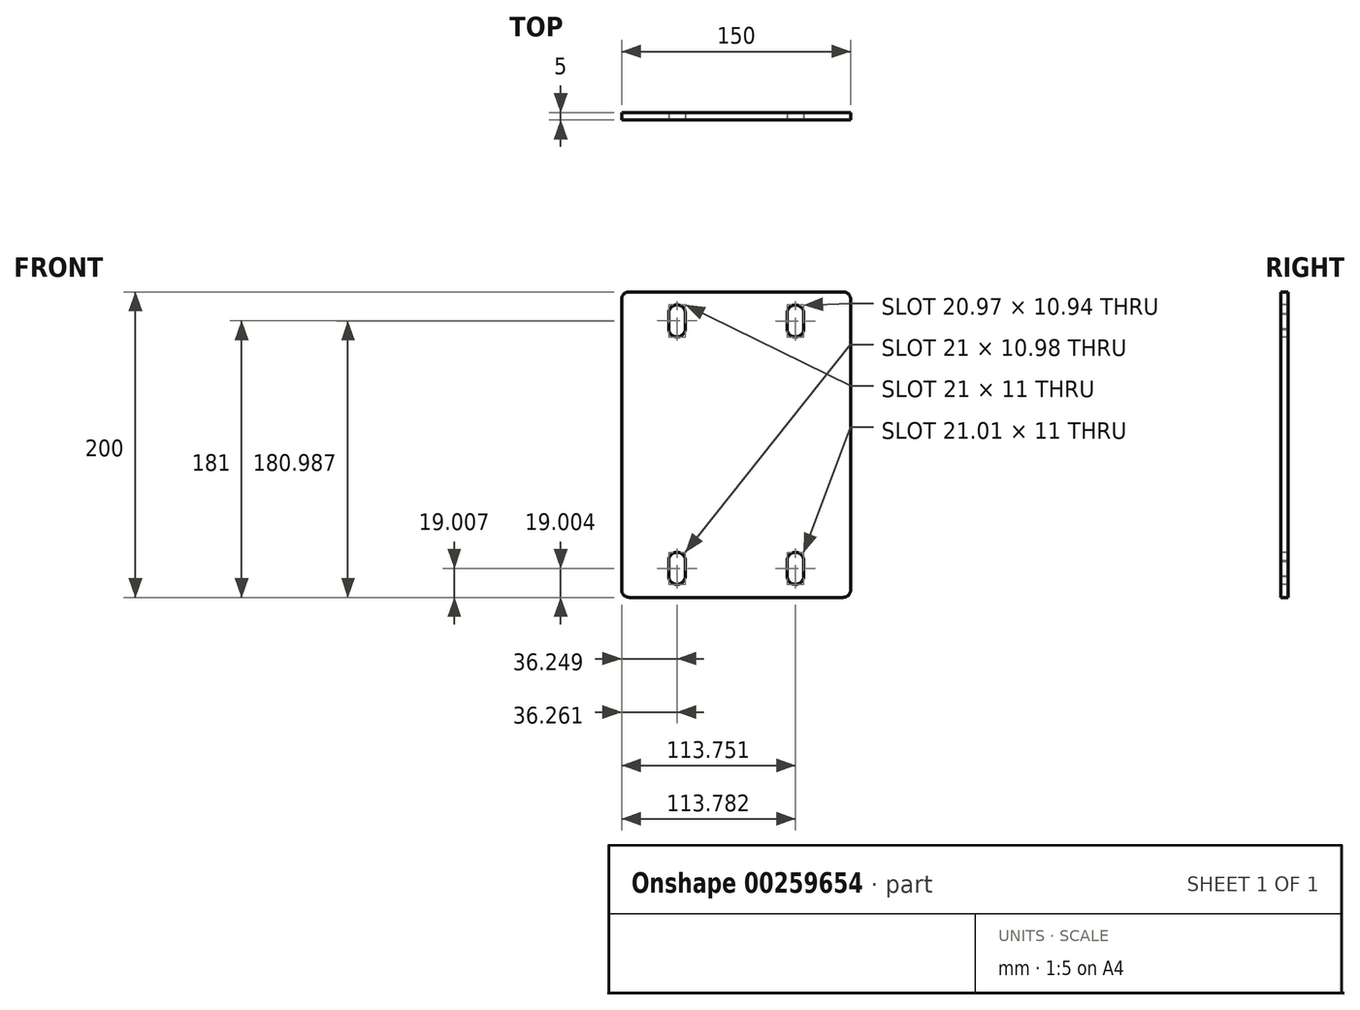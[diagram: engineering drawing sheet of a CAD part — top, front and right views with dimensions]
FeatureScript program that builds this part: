
annotation { "Feature Type Name" : "Feature", "Feature Type Description" : "" }
export const myFeature = defineFeature(function(context is Context, id is Id, definition is map)
    precondition{}
    {
        {
            var Q0;
            Q0=qCreatedBy(makeId("Front.planeOp"),FACE);
            var sketch = newSketch(context, id + "F0", { "sketchPlane" : qUnion([Q0])});
            skLineSegment(sketch, "E0.rect.bottom", {"start": v(-70, 100) * mm, "end": v(70, 100) * mm});
            skLineSegment(sketch, "E0.rect.top", {"start": v(-70, -100) * mm, "end": v(70, -100) * mm});
            skLineSegment(sketch, "E0.rect.left", {"start": v(-75, 95) * mm, "end": v(-75, -95) * mm});
            skLineSegment(sketch, "E0.rect.right", {"start": v(75, 95) * mm, "end": v(75, -95) * mm});
            skPoint(sketch, "E1.visualSharp", {"position": v(-75, 100) * mm});
            skArc(sketch, "E1.filletArc", {"start": v(-70, 100) * mm, "mid": v(-73.54, 98.54) * mm, "end": v(-75, 95) * mm});
            skPoint(sketch, "E2.visualSharp", {"position": v(-75, -100) * mm});
            skArc(sketch, "E2.filletArc", {"start": v(-75, -95) * mm, "mid": v(-73.54, -98.54) * mm, "end": v(-70, -100) * mm});
            skPoint(sketch, "E3.visualSharp", {"position": v(75, -100) * mm});
            skArc(sketch, "E3.filletArc", {"start": v(70, -100) * mm, "mid": v(73.54, -98.54) * mm, "end": v(75, -95) * mm});
            skPoint(sketch, "E4.visualSharp", {"position": v(75, 100) * mm});
            skArc(sketch, "E4.filletArc", {"start": v(75, 95) * mm, "mid": v(73.54, 98.54) * mm, "end": v(70, 100) * mm});
            skSolve(sketch);
        }
        {
            var Q0;
            Q0=qSketchRegion(id+"F0",true);
            extrude(context, id + "F1", {"entities" : qUnion([Q0]), "depth" : 5 * mm});
        }
        {
            var Q0;
            Q0=makeQuery(id+"F1.opExtrude","CAP_FACE",FACE,{"disambiguationData":[OSD([sQuery(id+"F0.wireOp",EDGE,"E0.rect.bottom"),sQuery(id+"F0.wireOp",EDGE,"E0.rect.top"),sQuery(id+"F0.wireOp",EDGE,"E0.rect.left"),sQuery(id+"F0.wireOp",EDGE,"E0.rect.right"),sQuery(id+"F0.wireOp",EDGE,"E1.filletArc"),sQuery(id+"F0.wireOp",EDGE,"E2.filletArc"),sQuery(id+"F0.wireOp",EDGE,"E3.filletArc"),sQuery(id+"F0.wireOp",EDGE,"E4.filletArc")])],"isStart":false});
            var sketch = newSketch(context, id + "F2", { "sketchPlane" : qUnion([Q0])});
            skLineSegment(sketch, "E5.rect.right", {"start": v(38.75, 86) * mm, "end": v(38.76, 85.98) * mm});
            skPoint(sketch, "E5.rect.middle", {"position": v(0, 0) * mm});
            skLineSegment(sketch, "E6", {"start": v(-44.24, 75.72) * mm, "end": v(-44.25, 86) * mm});
            skLineSegment(sketch, "E7", {"start": v(-33.25, 86) * mm, "end": v(-33.25, 76) * mm});
            skArc(sketch, "E8.trimOffspring", {"start": v(-44.24, 76.28) * mm, "mid": v(-38.89, 70.5) * mm, "end": v(-33.25, 76) * mm});
            skArc(sketch, "E9.trimOffspring", {"start": v(-33.25, 86) * mm, "mid": v(-38.75, 91.5) * mm, "end": v(-44.25, 86) * mm});
            skArc(sketch, "E10", {"start": v(33.31, 76.82) * mm, "mid": v(38.33, 70.5) * mm, "end": v(44.25, 75.99) * mm});
            skArc(sketch, "E11", {"start": v(33.25, -85.89) * mm, "mid": v(38.7, -91.5) * mm, "end": v(44.25, -86) * mm});
            skArc(sketch, "E12", {"start": v(-44.23, -85.51) * mm, "mid": v(-39, -91.5) * mm, "end": v(-33.25, -86) * mm});
            skLineSegment(sketch, "E13", {"start": v(-44.23, -76.5) * mm, "end": v(-44.23, -86.49) * mm});
            skLineSegment(sketch, "E14", {"start": v(33.31, 85.18) * mm, "end": v(33.31, 75.15) * mm});
            skLineSegment(sketch, "E15", {"start": v(44.25, 85.68) * mm, "end": v(44.25, 75.99) * mm});
            skArc(sketch, "E16.trimOffspring", {"start": v(44.25, 85.68) * mm, "mid": v(38.5, 91.47) * mm, "end": v(33.31, 85.18) * mm});
            skLineSegment(sketch, "E17", {"start": v(33.25, -86.11) * mm, "end": v(33.25, -75.76) * mm});
            skLineSegment(sketch, "E18", {"start": v(44.25, -75.93) * mm, "end": v(44.25, -86) * mm});
            skArc(sketch, "E19.trimOffspring", {"start": v(44.25, -76.06) * mm, "mid": v(38.67, -70.49) * mm, "end": v(33.25, -76.21) * mm});
            skLineSegment(sketch, "E20", {"start": v(-33.25, -76.02) * mm, "end": v(-33.25, -86) * mm});
            skArc(sketch, "E21.trimOffspring", {"start": v(-33.25, -76.02) * mm, "mid": v(-38.99, -70.5) * mm, "end": v(-44.23, -76.5) * mm});
            skSolve(sketch);
        }
        {
            var Q0;
            {var subQ3=sQuery(id+"F2.wireOp",EDGE,"E7");Q0=makeQuery(id+"F2.imprint","IMPRINT",FACE,{"disambiguationData":[TD([[makeQuery(id+"F2.imprint","IMPRINT",EDGE,{"derivedFrom":subQ3}),-1.0]])]});}
            var Q1;
            {var subQ0=sQuery(id+"F2.wireOp",EDGE,"E15");Q1=makeQuery(id+"F2.imprint","IMPRINT",FACE,{"disambiguationData":[TD([[makeQuery(id+"F2.imprint","IMPRINT",EDGE,{"derivedFrom":subQ0}),-1.0]])]});}
            var Q2;
            {var subQ0=sQuery(id+"F2.wireOp",EDGE,"E20");Q2=makeQuery(id+"F2.imprint","IMPRINT",FACE,{"disambiguationData":[TD([[makeQuery(id+"F2.imprint","IMPRINT",EDGE,{"derivedFrom":subQ0}),-1.0]])]});}
            var Q3;
            {var subQ3=sQuery(id+"F2.wireOp",EDGE,"E19.trimOffspring");Q3=makeQuery(id+"F2.imprint","IMPRINT",FACE,{"disambiguationData":[TD([[makeQuery(id+"F2.imprint","IMPRINT",EDGE,{"derivedFrom":subQ3}),1.0]])]});}
            extrude(context, id + "F3", {"entities" : qUnion([Q0, Q1, Q2, Q3]), "operationType" : NewBodyOperationType.REMOVE, "oppositeDirection" : true, "depth" : 25 * mm});
        }
    });
